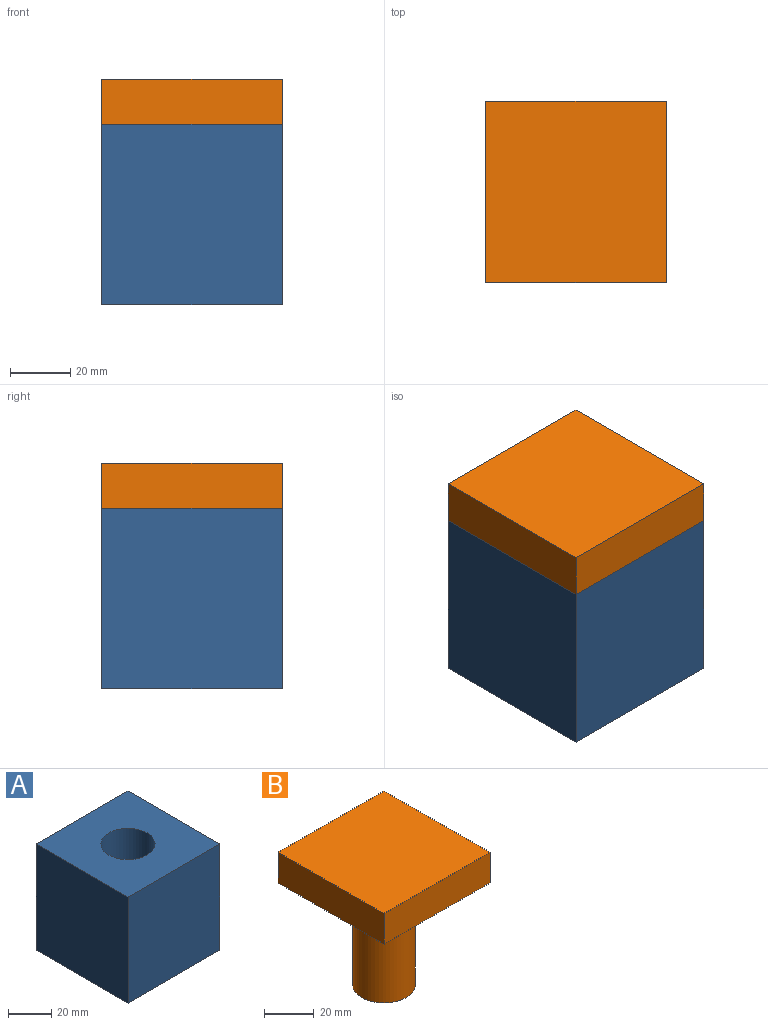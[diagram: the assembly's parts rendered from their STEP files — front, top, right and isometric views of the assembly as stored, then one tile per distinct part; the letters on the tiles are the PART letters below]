
ASSEMBLY  parts=2 mates=1
PART A: 8 faces, bbox 60x60x60 mm
  f0: plane 60x60mm, normal (-1,0,0), area 3600mm2, adj f1,f3,f4,f5
  f1: plane 60x60mm, normal (0,-1,0), area 3600mm2, adj f0,f2,f4,f5
  f2: plane 60x60mm, normal (1,0,0), area 3600mm2, adj f1,f3,f4,f5
  f3: plane 60x60mm, normal (0,1,0), area 3600mm2, adj f0,f2,f4,f5
  f4: plane 60x60mm, normal (0,0,1), area 3109.1mm2, adj f0,f1,f2,f3,f6
  f5: plane 60x60mm, normal (0,0,-1), area 3600mm2, adj f0,f1,f2,f3
  f6: cylinder r=12.5mm len=50mm, axis (0,0,1), area 3927mm2, adj f4,f7
  f7: plane 25x25mm, normal (0,0,1), area 490.9mm2, adj f6
PART B: 8 faces, bbox 60x60x65 mm
  f0: plane 60x15mm, normal (-1,0,0), area 900mm2, adj f1,f3,f4,f5
  f1: plane 60x15mm, normal (0,-1,0), area 900mm2, adj f0,f2,f4,f5
  f2: plane 60x15mm, normal (1,0,0), area 900mm2, adj f1,f3,f4,f5
  f3: plane 60x15mm, normal (0,1,0), area 900mm2, adj f0,f2,f4,f5
  f4: plane 60x60mm, normal (0,0,-1), area 3109.1mm2, adj f0,f1,f2,f3,f6
  f5: plane 60x60mm, normal (0,0,1), area 3600mm2, adj f0,f1,f2,f3
  f6: cylinder r=12.5mm len=50mm, axis (0,0,1), area 3927mm2, adj f4,f7
  f7: plane 25x25mm, normal (0,0,-1), area 490.9mm2, adj f6
PLACE A t=(-26.46,-10.73,-25.49)mm
PLACE B t=(-26.46,-10.73,-80.49)mm
MATE slider B.f6 <-> A.f6  axis (0,0,-1) through (3.54,19.27,-15.49)mm
